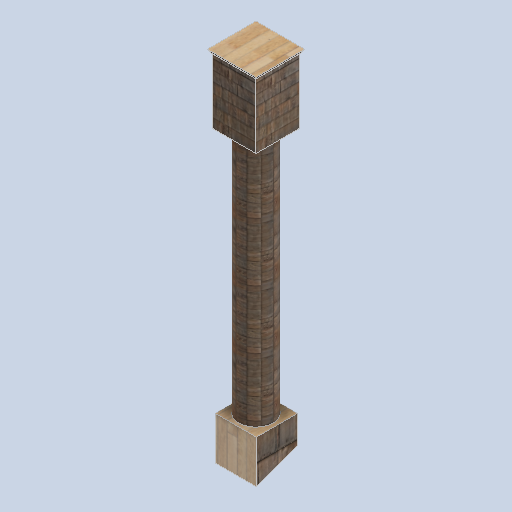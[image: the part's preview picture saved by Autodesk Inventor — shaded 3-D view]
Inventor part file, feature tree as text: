
AUTODESK INVENTOR PART (.ipt)
format: ipt  version: 2024.2 (Build 282272000, 272)  size: 175,616 bytes
history: native  units: in
note: dims shown in document units (in); Inventor stores cm internally (conversion verified against a paired STEP export)
features: sketch x5, other x3, plane x1
ambient origin geometry x8: Origin, YZ Plane, XZ Plane, XY Plane, X Axis, Y Axis, Z Axis, Center Point
bodies: Solid1 (feature_tree)
feature tree (9):
  other  "side_pillar_01.ipt"
  other  "Solid1::side_pillar_01.ipt"
  other  "TaggingFeature1"
  sketch  "Sketch1"  dims[d0=0.3937in]
  sketch  "Sketch2"
  sketch  "Sketch3"
  sketch  "Sketch4"
  sketch  "Sketch5"
  plane  "Work Plane3"
